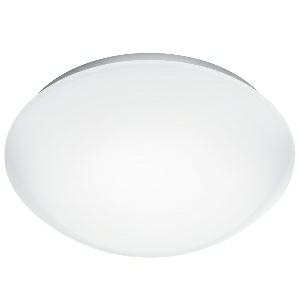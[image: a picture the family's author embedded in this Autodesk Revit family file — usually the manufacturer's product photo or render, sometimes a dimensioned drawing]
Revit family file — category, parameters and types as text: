
# Revit family: rs_pro_led_p3_056148
name_source: partatom
category: Leuchten
revit_build: Autodesk Revit 2016 (Build: 20190508_0715(x64)
units: mm (PartAtom-declared; Revit-internal decimal feet)

## family parameters
Basisbauteil = Fläche
Beim Laden mit Abzugskörper schneiden = Nein
Bemaßung runder Anschluss = Durchmesser verwenden
Gemeinsam genutzt = Nein
Lichtquelle = Nein
Raumberechnungspunkt = Nein
Teiletyp = Normal

## types (1)
- RS PRO LED P3 (1 x , 2210 lm, 3000 K)
    Beschreibung = Dimensions (Ø x H): 400 x 142 mm; Mains power supply: 220 – 240 V / 50 – 60 Hz; Sensor Technology: High frequency; Transmitter power: < 1 mW; HF-system: 5,8 GHz; Output: 20 W; Interconnection: Yes; Type of interconnection: Master/master; Luminous flux: 2210 lm; Colour temperature: 3000 K; Colour variation LED: SDCM3; Colour Rendering Index CRI: 80-89; With lamp: Yes, STEINEL LED system; Lamp: LED cannot be replaced; LED life expectancy (max. °C): 50000 h; Drop in luminous flux in accordance with LM80: L80B10; Base: without; LED cooling system: Passive Thermo Control; With motion detector: Yes; Detection: also through glass, wood and stud walls; Detection angle: 360 °; Angle of aperture: 160 °; Capability of masking out individual segments: Yes; Electronic scalability: Yes; Mechanical scalability: No; Reach, radial: Ø 8 m (50 m²); Reach, tangential: Ø 8 m (50 m²); Continuous light: selectable, 4h; Photo-cell controller: Yes; Twilight setting: 2 – 2000 lx; Time setting: 5 sec – 15 min; Basic light level function: Yes; Basic light level function time: 10/30 min, all night; Soft light start: Yes; Impact resistance: IK03; IP-rating: IP54; Protection class: II; Ambient temperature: 10 – 40 °C; Housing material: Plastic; Cover material: Plastic, opal; Manufacturer's Warranty: 5 years; Settings via: Potentiometers; With remote control: No; Version: warm white; PU1, EAN: 4007841056148
    CIE Flux Codes = 39 67 87 85 100
    Color Rendering = 80-89
    Color Temperature = 3000 K
    Frequency = 50 Hz, 60 Hz
    Height = 0 mm  [stored 0 ft]
    Hersteller = Steinel
    Lamp Light Flux = 2210 lm
    Lamp count = 1
    Lampe = 1 x
    Length = 400 mm
    Luminous efficacy = 111 lm/W
    ModVariant = Nein
    Modell = 056148
    Mounting Type = Surface mounted
    Number of Poles = 1
    OnlyDefault = Ja
    Power Factor = 1
    Product Name = RS PRO LED P3
    Product group = Sensor-switched indoor light
    ProductGroupID = 30
    Protection Class = Protection class II
    Protection Degree = IP 54
    RlxData = <blob elided: 39005 chars, md5=8bbc0178>
    Scheinlast = 20 VA
    Socket = socket
    Standby Power = 0 W
    System Light Flux = 2210 lm
    System Power = 20 W
    Typenbild = produkt1_056148.jpg
    Typenkommentare = Product without accessories
    URL = http://relux.com
    VarID = ---
    Voltage = 0 V
    Vorgabe-Ansicht = 1800 mm
    Weight = 0.00 kg
    Width = 0 mm  [stored 0 ft]

note: [stored X ft] marks values corroborated as IEEE doubles in the binary element streams (Revit-internal decimal feet)

## geometry (parser evidence)
native form markers: Sweep x14
no freeform markers — native parametric forms only
